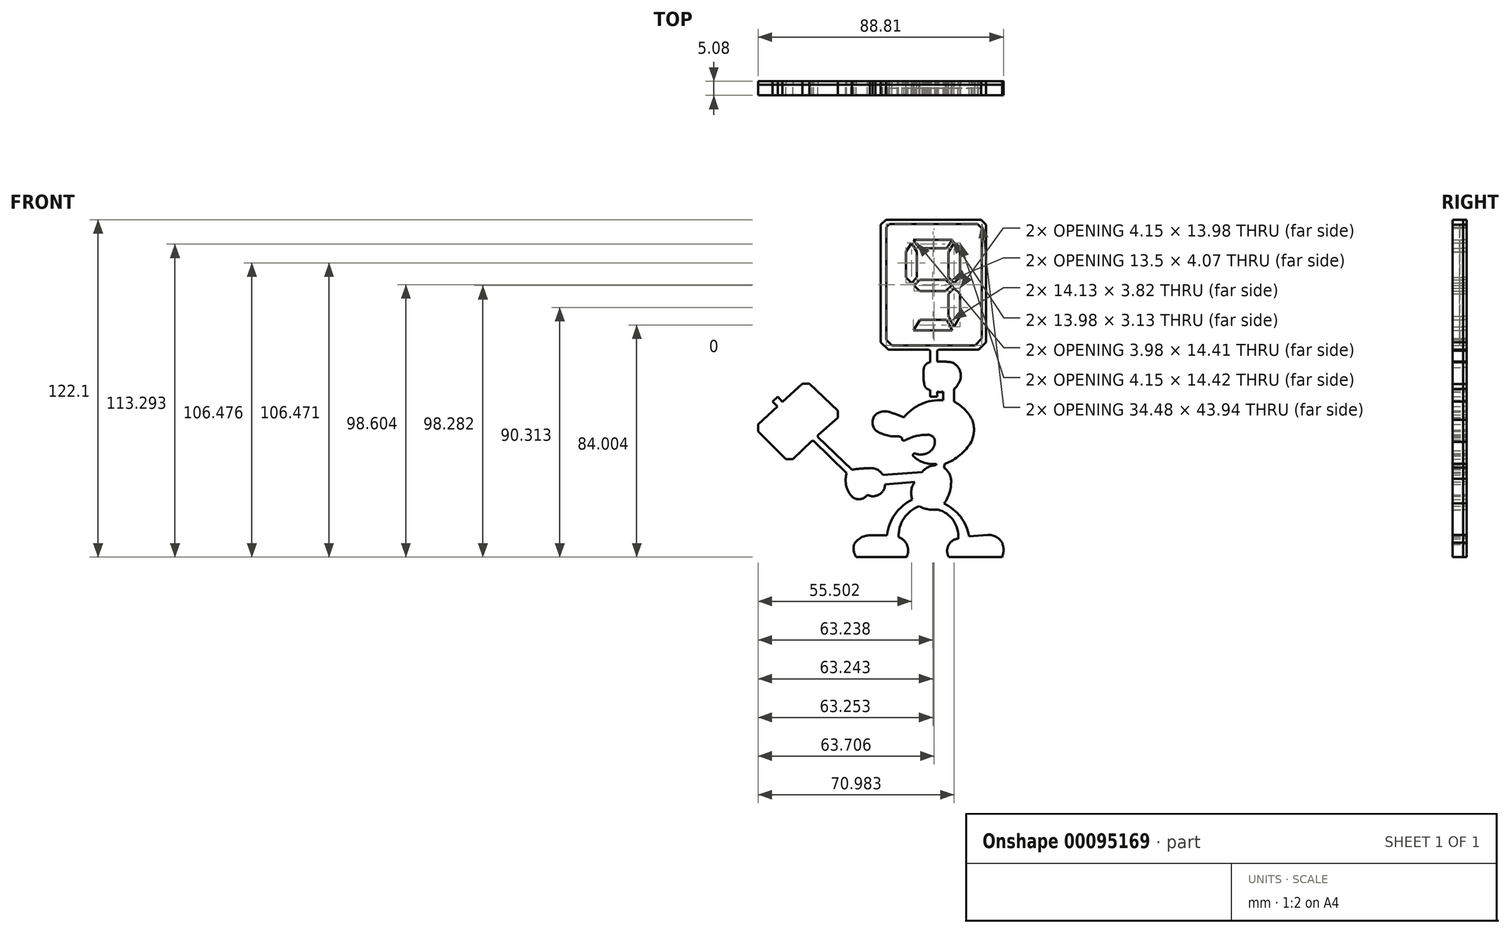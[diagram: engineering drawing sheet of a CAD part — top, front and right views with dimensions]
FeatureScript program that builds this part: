
annotation { "Feature Type Name" : "Feature", "Feature Type Description" : "" }
export const myFeature = defineFeature(function(context is Context, id is Id, definition is map)
    precondition{}
    {
        {
            var Q0;
            Q0=qCreatedBy(makeId("Front.planeOp"),FACE);
            var sketch = newSketch(context, id + "F0", { "sketchPlane" : qUnion([Q0])});
            skLineSegment(sketch, "E0", {"start": v(-24.4, 14.37) * mm, "end": v(-21.86, 14.37) * mm});
            skLineSegment(sketch, "E1", {"start": v(-21.86, 14.37) * mm, "end": v(-11.65, 4.52) * mm});
            skLineSegment(sketch, "E2", {"start": v(-11.65, 4.52) * mm, "end": v(-11.65, 1.98) * mm});
            skLineSegment(sketch, "E3", {"start": v(-24.4, 14.37) * mm, "end": v(-31.63, 7.75) * mm});
            skLineSegment(sketch, "E4", {"start": v(-31.63, 7.75) * mm, "end": v(-33.34, 9.62) * mm});
            skLineSegment(sketch, "E5", {"start": v(-33.34, 9.62) * mm, "end": v(-35.22, 7.9) * mm});
            skLineSegment(sketch, "E6", {"start": v(-35.22, 7.9) * mm, "end": v(-33.5, 6.03) * mm});
            skLineSegment(sketch, "E7", {"start": v(-33.5, 6.03) * mm, "end": v(-40.48, -0.37) * mm});
            skLineSegment(sketch, "E8", {"start": v(-40.48, -0.37) * mm, "end": v(-40.48, -2.9) * mm});
            skLineSegment(sketch, "E9", {"start": v(-40.48, -2.9) * mm, "end": v(-30.45, -12.94) * mm});
            skLineSegment(sketch, "E10", {"start": v(-30.45, -12.94) * mm, "end": v(-27.91, -12.94) * mm});
            skLineSegment(sketch, "E11", {"start": v(-27.91, -12.94) * mm, "end": v(-21, -6.38) * mm});
            skLineSegment(sketch, "E12", {"start": v(-21, -6.38) * mm, "end": v(-20.37, -6.38) * mm});
            skLineSegment(sketch, "E13", {"start": v(-20.37, -6.38) * mm, "end": v(-8.39, -18) * mm});
            skLineSegment(sketch, "E14", {"start": v(-11.65, 1.98) * mm, "end": v(-18.8, -4.32) * mm});
            skLineSegment(sketch, "E15", {"start": v(-18.8, -4.32) * mm, "end": v(-18.8, -4.95) * mm});
            skLineSegment(sketch, "E16", {"start": v(-18.8, -4.95) * mm, "end": v(-6.57, -16.8) * mm});
            skArc(sketch, "E17", {"start": v(-8.39, -18) * mm, "mid": v(-8.63, -22.18) * mm, "end": v(-6.9, -26) * mm});
            skArc(sketch, "E18", {"start": v(-6.9, -26) * mm, "mid": v(-3.9, -27.5) * mm, "end": v(-0.98, -25.87) * mm});
            skArc(sketch, "E19", {"start": v(-0.98, -25.87) * mm, "mid": v(3.31, -25.8) * mm, "end": v(5.5, -22.09) * mm});
            skArc(sketch, "E20", {"start": v(4.68, -18.71) * mm, "mid": v(2.7, -16.78) * mm, "end": v(0, -16.22) * mm});
            skArc(sketch, "E21", {"start": v(0, -16.22) * mm, "mid": v(-3.3, -16.4) * mm, "end": v(-6.57, -16.8) * mm});
            skLineSegment(sketch, "E22", {"start": v(5.5, -22.09) * mm, "end": v(16.16, -21.27) * mm});
            skLineSegment(sketch, "E23", {"start": v(4.68, -18.71) * mm, "end": v(18.9, -17.62) * mm});
            skArc(sketch, "E24", {"start": v(23.92, -15.16) * mm, "mid": v(21.14, -15.83) * mm, "end": v(18.9, -17.62) * mm});
            skArc(sketch, "E25", {"start": v(16.16, -21.27) * mm, "mid": v(14.99, -24.34) * mm, "end": v(15.36, -27.61) * mm});
            skArc(sketch, "E26", {"start": v(15.36, -27.61) * mm, "mid": v(9.1, -32.89) * mm, "end": v(6.19, -40.54) * mm});
            skLineSegment(sketch, "E27", {"start": v(6.19, -40.54) * mm, "end": v(0, -40.54) * mm});
            skArc(sketch, "E28", {"start": v(0, -40.54) * mm, "mid": v(-3.28, -41.41) * mm, "end": v(-5.7, -43.8) * mm});
            skArc(sketch, "E29", {"start": v(-5.7, -43.8) * mm, "mid": v(-5.84, -46.17) * mm, "end": v(-4.97, -48.37) * mm});
            skLineSegment(sketch, "E30", {"start": v(-4.97, -48.37) * mm, "end": v(13.24, -48.37) * mm});
            skArc(sketch, "E31", {"start": v(17.86, -30) * mm, "mid": v(12.3, -34.38) * mm, "end": v(10.44, -41.21) * mm});
            skArc(sketch, "E32", {"start": v(13.24, -48.37) * mm, "mid": v(13.48, -44.15) * mm, "end": v(10.44, -41.21) * mm});
            skArc(sketch, "E33", {"start": v(17.86, -30) * mm, "mid": v(21.1, -31.15) * mm, "end": v(24.55, -31.2) * mm});
            skArc(sketch, "E34", {"start": v(31.92, -41.73) * mm, "mid": v(30.16, -35.12) * mm, "end": v(24.55, -31.2) * mm});
            skArc(sketch, "E35", {"start": v(31.92, -41.73) * mm, "mid": v(28.42, -44.16) * mm, "end": v(28.55, -48.42) * mm});
            skLineSegment(sketch, "E36", {"start": v(28.55, -48.42) * mm, "end": v(47.8, -48.42) * mm});
            skArc(sketch, "E37", {"start": v(47.8, -48.42) * mm, "mid": v(48.33, -45.8) * mm, "end": v(47.8, -43.18) * mm});
            skArc(sketch, "E38", {"start": v(47.8, -43.18) * mm, "mid": v(45.59, -41.04) * mm, "end": v(42.58, -40.4) * mm});
            skLineSegment(sketch, "E39", {"start": v(42.58, -40.4) * mm, "end": v(35.9, -40.92) * mm});
            skArc(sketch, "E40", {"start": v(35.9, -40.92) * mm, "mid": v(32.81, -33.85) * mm, "end": v(26.8, -29.02) * mm});
            skArc(sketch, "E41", {"start": v(26.8, -29.02) * mm, "mid": v(28.88, -24.8) * mm, "end": v(29.34, -20.11) * mm});
            skArc(sketch, "E42", {"start": v(29.34, -20.11) * mm, "mid": v(28.45, -17.81) * mm, "end": v(26.75, -16.02) * mm});
            skLineSegment(sketch, "E43", {"start": v(26.75, -16.02) * mm, "end": v(27.2, -14.67) * mm});
            skLineSegment(sketch, "E44", {"start": v(23.92, -15.16) * mm, "end": v(24.08, -14.67) * mm});
            skArc(sketch, "E45", {"start": v(15.64, -11.86) * mm, "mid": v(19.54, -14.23) * mm, "end": v(24.08, -14.67) * mm});
            skArc(sketch, "E46", {"start": v(16.63, -11.06) * mm, "mid": v(15.8, -11.04) * mm, "end": v(15.64, -11.86) * mm});
            skArc(sketch, "E47", {"start": v(16.63, -11.06) * mm, "mid": v(18.4, -11.3) * mm, "end": v(20.17, -11.06) * mm});
            skArc(sketch, "E48", {"start": v(20.17, -11.06) * mm, "mid": v(21.23, -10.57) * mm, "end": v(22.15, -9.86) * mm});
            skArc(sketch, "E49", {"start": v(22.15, -9.86) * mm, "mid": v(23.3, -8.08) * mm, "end": v(23.43, -5.97) * mm});
            skArc(sketch, "E50", {"start": v(23.43, -5.97) * mm, "mid": v(22.43, -4.56) * mm, "end": v(20.75, -4.14) * mm});
            skArc(sketch, "E51", {"start": v(20.75, -4.14) * mm, "mid": v(16.7, -4.62) * mm, "end": v(12.88, -6.05) * mm});
            skArc(sketch, "E52", {"start": v(2, -2.46) * mm, "mid": v(5.72, -4.24) * mm, "end": v(9.83, -4.73) * mm});
            skArc(sketch, "E53", {"start": v(2, 3.1) * mm, "mid": v(0.93, 0.32) * mm, "end": v(2, -2.46) * mm});
            skArc(sketch, "E54", {"start": v(7.25, 4.03) * mm, "mid": v(4.5, 4.27) * mm, "end": v(2, 3.1) * mm});
            skArc(sketch, "E55", {"start": v(12.32, 2.17) * mm, "mid": v(9.8, 3.15) * mm, "end": v(7.25, 4.03) * mm});
            skArc(sketch, "E56", {"start": v(26.47, 8.35) * mm, "mid": v(18.62, 7.02) * mm, "end": v(12.32, 2.17) * mm});
            skArc(sketch, "E57", {"start": v(11.6, -5.25) * mm, "mid": v(10.76, -4.82) * mm, "end": v(9.83, -4.73) * mm});
            skArc(sketch, "E58", {"start": v(11.6, -6.03) * mm, "mid": v(11.65, -5.64) * mm, "end": v(11.6, -5.25) * mm});
            skArc(sketch, "E59", {"start": v(11.6, -6.03) * mm, "mid": v(12.24, -6.22) * mm, "end": v(12.88, -6.05) * mm});
            skLineSegment(sketch, "E60", {"start": v(30.42, 7.87) * mm, "end": v(30.42, 12.42) * mm});
            skLineSegment(sketch, "E61", {"start": v(26.47, 8.35) * mm, "end": v(26.47, 11.39) * mm});
            skLineSegment(sketch, "E62", {"start": v(24.8, 26.69) * mm, "end": v(39.36, 26.69) * mm});
            skLineSegment(sketch, "E63", {"start": v(39.36, 26.69) * mm, "end": v(42.05, 29.38) * mm});
            skLineSegment(sketch, "E64", {"start": v(42.05, 29.38) * mm, "end": v(42.05, 73.68) * mm});
            skLineSegment(sketch, "E65", {"start": v(42.05, 73.68) * mm, "end": v(3.95, 73.68) * mm});
            skLineSegment(sketch, "E66", {"start": v(3.95, 26.69) * mm, "end": v(21.32, 26.69) * mm});
            skLineSegment(sketch, "E67", {"start": v(21.32, 26.69) * mm, "end": v(21.77, 26.24) * mm});
            skLineSegment(sketch, "E68", {"start": v(21.77, 26.24) * mm, "end": v(21.77, 9.6) * mm});
            skLineSegment(sketch, "E69", {"start": v(21.77, 9.6) * mm, "end": v(24.35, 9.6) * mm});
            skLineSegment(sketch, "E70", {"start": v(24.35, 9.6) * mm, "end": v(24.35, 26.24) * mm});
            skLineSegment(sketch, "E71", {"start": v(24.8, 26.69) * mm, "end": v(24.35, 26.24) * mm});
            skArc(sketch, "E72", {"start": v(20.34, 12.68) * mm, "mid": v(23.3, 11.57) * mm, "end": v(26.47, 11.39) * mm});
            skArc(sketch, "E73", {"start": v(19.56, 20.16) * mm, "mid": v(19.34, 17.1) * mm, "end": v(19.68, 14.07) * mm});
            skArc(sketch, "E74", {"start": v(19.68, 14.07) * mm, "mid": v(19.93, 13.34) * mm, "end": v(20.34, 12.68) * mm});
            skLineSegment(sketch, "E75", {"start": v(40.26, 73.68) * mm, "end": v(42.05, 71.88) * mm});
            skLineSegment(sketch, "E76", {"start": v(3.95, 26.69) * mm, "end": v(3.95, 73.68) * mm});
            skLineSegment(sketch, "E77", {"start": v(5.75, 73.68) * mm, "end": v(3.95, 71.88) * mm});
            skLineSegment(sketch, "E78", {"start": v(3.95, 29.38) * mm, "end": v(6.65, 26.69) * mm});
            skLineSegment(sketch, "E79", {"start": v(42.05, 73.68) * mm, "end": v(42.05, 26.69) * mm});
            skLineSegment(sketch, "E80", {"start": v(42.05, 26.69) * mm, "end": v(39.36, 26.69) * mm});
            skLineSegment(sketch, "E81", {"start": v(38.9, 72.15) * mm, "end": v(40.47, 70.6) * mm});
            skLineSegment(sketch, "E82", {"start": v(40.47, 70.6) * mm, "end": v(40.47, 30.67) * mm});
            skLineSegment(sketch, "E83", {"start": v(40.47, 30.67) * mm, "end": v(38.01, 28.21) * mm});
            skLineSegment(sketch, "E84", {"start": v(38.01, 28.21) * mm, "end": v(8, 28.21) * mm});
            skLineSegment(sketch, "E85", {"start": v(8, 28.21) * mm, "end": v(5.99, 30.22) * mm});
            skLineSegment(sketch, "E86", {"start": v(5.99, 30.22) * mm, "end": v(5.99, 71.04) * mm});
            skLineSegment(sketch, "E87", {"start": v(5.99, 71.04) * mm, "end": v(7.1, 72.15) * mm});
            skLineSegment(sketch, "E88", {"start": v(7.1, 72.15) * mm, "end": v(38.9, 72.15) * mm});
            skArc(sketch, "E89", {"start": v(27.2, -14.67) * mm, "mid": v(32.6, -11.48) * mm, "end": v(36.69, -6.71) * mm});
            skArc(sketch, "E90", {"start": v(36.69, -6.71) * mm, "mid": v(37.64, -2.76) * mm, "end": v(37, 1.25) * mm});
            skArc(sketch, "E91", {"start": v(37, 1.25) * mm, "mid": v(34.24, 5.1) * mm, "end": v(30.42, 7.87) * mm});
            skLineSegment(sketch, "E92", {"start": v(15.77, 66.44) * mm, "end": v(29.75, 66.44) * mm});
            skLineSegment(sketch, "E93", {"start": v(29.75, 66.44) * mm, "end": v(27.76, 63.3) * mm});
            skLineSegment(sketch, "E94", {"start": v(27.76, 63.3) * mm, "end": v(17.76, 63.3) * mm});
            skLineSegment(sketch, "E95", {"start": v(17.76, 63.3) * mm, "end": v(15.77, 66.44) * mm});
            skLineSegment(sketch, "E96", {"start": v(30.5, 65.26) * mm, "end": v(28.43, 62) * mm});
            skLineSegment(sketch, "E97", {"start": v(28.43, 62) * mm, "end": v(28.43, 52.88) * mm});
            skLineSegment(sketch, "E98", {"start": v(28.43, 52.88) * mm, "end": v(30.5, 50.84) * mm});
            skLineSegment(sketch, "E99", {"start": v(30.5, 50.84) * mm, "end": v(32.58, 52.88) * mm});
            skLineSegment(sketch, "E100", {"start": v(32.58, 52.88) * mm, "end": v(32.58, 62) * mm});
            skLineSegment(sketch, "E101", {"start": v(32.58, 62) * mm, "end": v(30.5, 65.26) * mm});
            skLineSegment(sketch, "E102", {"start": v(29.5, 49.86) * mm, "end": v(27.43, 51.9) * mm});
            skLineSegment(sketch, "E103", {"start": v(27.43, 51.9) * mm, "end": v(18.05, 51.9) * mm});
            skLineSegment(sketch, "E104", {"start": v(18.05, 51.9) * mm, "end": v(16.01, 49.86) * mm});
            skLineSegment(sketch, "E105", {"start": v(16.01, 49.86) * mm, "end": v(18.05, 47.83) * mm});
            skLineSegment(sketch, "E106", {"start": v(18.05, 47.83) * mm, "end": v(27.43, 47.83) * mm});
            skLineSegment(sketch, "E107", {"start": v(27.43, 47.83) * mm, "end": v(29.5, 49.86) * mm});
            skLineSegment(sketch, "E108", {"start": v(17.01, 52.84) * mm, "end": v(15.02, 50.85) * mm});
            skLineSegment(sketch, "E109", {"start": v(15.02, 50.85) * mm, "end": v(13.03, 52.84) * mm});
            skLineSegment(sketch, "E110", {"start": v(13.03, 52.84) * mm, "end": v(13.03, 62.13) * mm});
            skLineSegment(sketch, "E111", {"start": v(13.03, 62.13) * mm, "end": v(15.02, 65.26) * mm});
            skLineSegment(sketch, "E112", {"start": v(15.02, 65.26) * mm, "end": v(17.01, 62.13) * mm});
            skLineSegment(sketch, "E113", {"start": v(17.01, 62.13) * mm, "end": v(17.01, 52.84) * mm});
            skLineSegment(sketch, "E114", {"start": v(29.84, 33.67) * mm, "end": v(27.76, 37.5) * mm});
            skLineSegment(sketch, "E115", {"start": v(27.76, 37.5) * mm, "end": v(18.09, 37.5) * mm});
            skLineSegment(sketch, "E116", {"start": v(18.09, 37.5) * mm, "end": v(15.71, 33.67) * mm});
            skLineSegment(sketch, "E117", {"start": v(15.71, 33.67) * mm, "end": v(29.84, 33.67) * mm});
            skLineSegment(sketch, "E118", {"start": v(30.5, 34.9) * mm, "end": v(28.43, 38.72) * mm});
            skLineSegment(sketch, "E119", {"start": v(28.43, 38.72) * mm, "end": v(28.43, 46.85) * mm});
            skLineSegment(sketch, "E120", {"start": v(28.43, 46.85) * mm, "end": v(30.5, 48.88) * mm});
            skLineSegment(sketch, "E121", {"start": v(30.5, 48.88) * mm, "end": v(32.58, 46.85) * mm});
            skLineSegment(sketch, "E122", {"start": v(32.58, 46.85) * mm, "end": v(32.58, 38.72) * mm});
            skLineSegment(sketch, "E123", {"start": v(32.58, 38.72) * mm, "end": v(30.5, 34.9) * mm});
            skLineSegment(sketch, "E124", {"start": v(28.43, 46.85) * mm, "end": v(32.58, 46.85) * mm});
            skLineSegment(sketch, "E125", {"start": v(13.03, 62.13) * mm, "end": v(15.77, 66.44) * mm});
            skLineSegment(sketch, "E126", {"start": v(32.58, 62) * mm, "end": v(29.75, 66.44) * mm});
            skLineSegment(sketch, "E127", {"start": v(13.03, 62.13) * mm, "end": v(17.01, 62.13) * mm});
            skLineSegment(sketch, "E128", {"start": v(28.43, 62) * mm, "end": v(32.58, 62) * mm});
            skLineSegment(sketch, "E129", {"start": v(18.05, 51.9) * mm, "end": v(18.05, 47.83) * mm});
            skLineSegment(sketch, "E130", {"start": v(29.84, 33.67) * mm, "end": v(32.58, 38.72) * mm});
            skLineSegment(sketch, "E131", {"start": v(27.76, 37.5) * mm, "end": v(28.95, 39.68) * mm});
            skLineSegment(sketch, "E132", {"start": v(32.58, 46.85) * mm, "end": v(27.43, 51.9) * mm});
            skLineSegment(sketch, "E133", {"start": v(28.43, 46.85) * mm, "end": v(24.6, 50.6) * mm});
            skLineSegment(sketch, "E134", {"start": v(18.05, 51.9) * mm, "end": v(14.3, 55.32) * mm});
            skLineSegment(sketch, "E135", {"start": v(27.43, 47.83) * mm, "end": v(32.58, 52.88) * mm});
            skLineSegment(sketch, "E136", {"start": v(17.01, 62.13) * mm, "end": v(19.33, 65.77) * mm});
            skLineSegment(sketch, "E137", {"start": v(28.43, 62) * mm, "end": v(25.65, 66.37) * mm});
            skLineSegment(sketch, "E138", {"start": v(27.43, 51.9) * mm, "end": v(30.99, 55.39) * mm});
            skLineSegment(sketch, "E139", {"start": v(30.5, 48.88) * mm, "end": v(30.5, 50.84) * mm});
            skArc(sketch, "E140", {"start": v(21.77, 22.1) * mm, "mid": v(20.4, 21.43) * mm, "end": v(19.56, 20.16) * mm});
            skArc(sketch, "E141", {"start": v(29.58, 22.1) * mm, "mid": v(25.67, 22.35) * mm, "end": v(21.77, 22.1) * mm});
            skArc(sketch, "E142", {"start": v(31.9, 14.23) * mm, "mid": v(32.67, 18.73) * mm, "end": v(29.58, 22.1) * mm});
            skArc(sketch, "E143", {"start": v(30.42, 12.42) * mm, "mid": v(31.29, 13.22) * mm, "end": v(31.9, 14.23) * mm});
            skLineSegment(sketch, "E144", {"start": v(15.02, 50.85) * mm, "end": v(16.01, 49.86) * mm});
            skSolve(sketch);
        }
        {
            var Q0;
            Q0=makeQuery(id+"F0.imprint","IMPRINT",FACE,{"disambiguationData":[TD([[makeQuery(id+"F0.imprint","IMPRINT",EDGE,{"derivedFrom":sQuery(id+"F0.wireOp",EDGE,"E0")}),-1.0]])]});
            var Q1;
            {var subQ3=sQuery(id+"F0.wireOp",EDGE,"E72");var subQ5=sQuery(id+"F0.wireOp",EDGE,"E70");var subQ6=makeQuery(id+"F0.imprint","INTERSECT",VERTEX,{"derivedFrom":[subQ5,subQ3]});Q1=makeQuery(id+"F0.imprint","IMPRINT",FACE,{"disambiguationData":[TD([[makeQuery(id+"F0.imprint","IMPRINT",EDGE,{"disambiguationData":[TD([[subQ6,-1.0]])],"derivedFrom":subQ5}),1.0]])]});}
            var Q2;
            Q2=makeQuery(id+"F0.imprint","IMPRINT",FACE,{"disambiguationData":[TD([[makeQuery(id+"F0.imprint","IMPRINT",EDGE,{"derivedFrom":sQuery(id+"F0.wireOp",EDGE,"E73")}),1.0]])]});
            var Q3;
            {var subQ0=sQuery(id+"F0.wireOp",EDGE,"E69");Q3=makeQuery(id+"F0.imprint","IMPRINT",FACE,{"disambiguationData":[TD([[makeQuery(id+"F0.imprint","IMPRINT",EDGE,{"derivedFrom":subQ0}),1.0]])]});}
            var Q4;
            Q4=makeQuery(id+"F0.imprint","IMPRINT",FACE,{"disambiguationData":[TD([[makeQuery(id+"F0.imprint","IMPRINT",EDGE,{"derivedFrom":sQuery(id+"F0.wireOp",EDGE,"E62")}),1.0]])]});
            var Q5;
            Q5=makeQuery(id+"F0.imprint","IMPRINT",FACE,{"disambiguationData":[TD([[makeQuery(id+"F0.imprint","IMPRINT",EDGE,{"derivedFrom":sQuery(id+"F0.wireOp",EDGE,"E114")}),1.0]])]});
            var Q6;
            {var subQ2=sQuery(id+"F0.wireOp",EDGE,"E118");Q6=makeQuery(id+"F0.imprint","IMPRINT",FACE,{"disambiguationData":[TD([[makeQuery(id+"F0.imprint","IMPRINT",EDGE,{"derivedFrom":subQ2}),-1.0]])]});}
            var Q7;
            {var subQ0=sQuery(id+"F0.wireOp",EDGE,"E120");Q7=makeQuery(id+"F0.imprint","IMPRINT",FACE,{"disambiguationData":[TD([[makeQuery(id+"F0.imprint","IMPRINT",EDGE,{"derivedFrom":subQ0}),-1.0]])]});}
            var Q8;
            {var subQ1=sQuery(id+"F0.wireOp",EDGE,"E103");Q8=makeQuery(id+"F0.imprint","IMPRINT",FACE,{"disambiguationData":[TD([[makeQuery(id+"F0.imprint","IMPRINT",EDGE,{"derivedFrom":subQ1}),1.0]])]});}
            var Q9;
            {var subQ0=sQuery(id+"F0.wireOp",EDGE,"E104");Q9=makeQuery(id+"F0.imprint","IMPRINT",FACE,{"disambiguationData":[TD([[makeQuery(id+"F0.imprint","IMPRINT",EDGE,{"derivedFrom":subQ0}),1.0]])]});}
            var Q10;
            {var subQ1=sQuery(id+"F0.wireOp",EDGE,"E108");Q10=makeQuery(id+"F0.imprint","IMPRINT",FACE,{"disambiguationData":[TD([[makeQuery(id+"F0.imprint","IMPRINT",EDGE,{"derivedFrom":subQ1}),-1.0]])]});}
            var Q11;
            {var subQ0=sQuery(id+"F0.wireOp",EDGE,"E112");Q11=makeQuery(id+"F0.imprint","IMPRINT",FACE,{"disambiguationData":[TD([[makeQuery(id+"F0.imprint","IMPRINT",EDGE,{"derivedFrom":subQ0}),-1.0]])]});}
            var Q12;
            Q12=makeQuery(id+"F0.imprint","IMPRINT",FACE,{"disambiguationData":[TD([[makeQuery(id+"F0.imprint","IMPRINT",EDGE,{"derivedFrom":sQuery(id+"F0.wireOp",EDGE,"E92")}),-1.0]])]});
            var Q13;
            {var subQ0=sQuery(id+"F0.wireOp",EDGE,"E96");Q13=makeQuery(id+"F0.imprint","IMPRINT",FACE,{"disambiguationData":[TD([[makeQuery(id+"F0.imprint","IMPRINT",EDGE,{"derivedFrom":subQ0}),1.0]])]});}
            var Q14;
            {var subQ1=sQuery(id+"F0.wireOp",EDGE,"E98");Q14=makeQuery(id+"F0.imprint","IMPRINT",FACE,{"disambiguationData":[TD([[makeQuery(id+"F0.imprint","IMPRINT",EDGE,{"derivedFrom":subQ1}),1.0]])]});}
            extrude(context, id + "F1", {"entities" : qUnion([Q0, Q1, Q2, Q3, Q4, Q5, Q6, Q7, Q8, Q9, Q10, Q11, Q12, Q13, Q14]), "depth" : 3.8 * mm});
        }
        {
            var Q0;
            Q0=makeQuery(id+"F0.imprint","IMPRINT",FACE,{"disambiguationData":[TD([[makeQuery(id+"F0.imprint","IMPRINT",EDGE,{"derivedFrom":sQuery(id+"F0.wireOp",EDGE,"E81")}),-1.0]])]});
            var Q1;
            {var subQ5=sQuery(id+"F0.wireOp",EDGE,"E98");Q1=makeQuery(id+"F0.imprint","IMPRINT",FACE,{"disambiguationData":[TD([[makeQuery(id+"F0.imprint","IMPRINT",EDGE,{"derivedFrom":subQ5}),-1.0]])]});}
            var Q2;
            {var subQ0=sQuery(id+"F0.wireOp",EDGE,"E139");Q2=makeQuery(id+"F0.imprint","IMPRINT",FACE,{"disambiguationData":[TD([[makeQuery(id+"F0.imprint","IMPRINT",EDGE,{"derivedFrom":subQ0}),1.0]])]});}
            var Q3;
            {var subQ0=sQuery(id+"F0.wireOp",EDGE,"E120");Q3=makeQuery(id+"F0.imprint","IMPRINT",FACE,{"disambiguationData":[TD([[makeQuery(id+"F0.imprint","IMPRINT",EDGE,{"derivedFrom":subQ0}),1.0]])]});}
            var Q4;
            {var subQ0=sQuery(id+"F0.wireOp",EDGE,"E114");Q4=makeQuery(id+"F0.imprint","IMPRINT",FACE,{"disambiguationData":[TD([[makeQuery(id+"F0.imprint","IMPRINT",EDGE,{"derivedFrom":subQ0}),-1.0]])]});}
            var Q5;
            {var subQ0=sQuery(id+"F0.wireOp",EDGE,"E104");Q5=makeQuery(id+"F0.imprint","IMPRINT",FACE,{"disambiguationData":[TD([[makeQuery(id+"F0.imprint","IMPRINT",EDGE,{"derivedFrom":subQ0}),-1.0]])]});}
            var Q6;
            {var subQ1=sQuery(id+"F0.wireOp",EDGE,"E103");Q6=makeQuery(id+"F0.imprint","IMPRINT",FACE,{"disambiguationData":[TD([[makeQuery(id+"F0.imprint","IMPRINT",EDGE,{"derivedFrom":subQ1}),-1.0]])]});}
            var Q7;
            {var subQ0=sQuery(id+"F0.wireOp",EDGE,"E95");Q7=makeQuery(id+"F0.imprint","IMPRINT",FACE,{"disambiguationData":[TD([[makeQuery(id+"F0.imprint","IMPRINT",EDGE,{"derivedFrom":subQ0}),1.0]])]});}
            var Q8;
            {var subQ1=sQuery(id+"F0.wireOp",EDGE,"E93");Q8=makeQuery(id+"F0.imprint","IMPRINT",FACE,{"disambiguationData":[TD([[makeQuery(id+"F0.imprint","IMPRINT",EDGE,{"derivedFrom":subQ1}),1.0]])]});}
            extrude(context, id + "F2", {"entities" : qUnion([Q0, Q1, Q2, Q3, Q4, Q5, Q6, Q7, Q8]), "depth" : 1.27 * mm});
        }
        {
            var Q0;
            Q0=makeQuery(id+"F1.opExtrude","CAP_FACE",FACE,{"disambiguationData":[OSD([sQuery(id+"F0.wireOp",EDGE,"E96"),sQuery(id+"F0.wireOp",EDGE,"E97"),sQuery(id+"F0.wireOp",EDGE,"E98"),sQuery(id+"F0.wireOp",EDGE,"E100"),sQuery(id+"F0.wireOp",EDGE,"E126"),sQuery(id+"F0.wireOp",EDGE,"E135")])],"isStart":true});
            var Q1;
            Q1=makeQuery(id+"F1.opExtrude","CAP_FACE",FACE,{"disambiguationData":[OSD([sQuery(id+"F0.wireOp",EDGE,"E92"),sQuery(id+"F0.wireOp",EDGE,"E93"),sQuery(id+"F0.wireOp",EDGE,"E94"),sQuery(id+"F0.wireOp",EDGE,"E95")])],"isStart":true});
            var Q2;
            Q2=makeQuery(id+"F1.opExtrude","CAP_FACE",FACE,{"disambiguationData":[OSD([sQuery(id+"F0.wireOp",EDGE,"E108"),sQuery(id+"F0.wireOp",EDGE,"E110"),sQuery(id+"F0.wireOp",EDGE,"E112"),sQuery(id+"F0.wireOp",EDGE,"E113"),sQuery(id+"F0.wireOp",EDGE,"nikI6qLt-cf0r-R0Sj-jdNE-G8wGwsvtiRU5"),sQuery(id+"F0.wireOp",EDGE,"E125")])],"isStart":true});
            var Q3;
            Q3=makeQuery(id+"F1.opExtrude","CAP_FACE",FACE,{"disambiguationData":[OSD([sQuery(id+"F0.wireOp",EDGE,"E103"),sQuery(id+"F0.wireOp",EDGE,"E104"),sQuery(id+"F0.wireOp",EDGE,"E106"),sQuery(id+"F0.wireOp",EDGE,"nikI6qLt-cf0r-R0Sj-jdNE-G8wGwsvtiRU5"),sQuery(id+"F0.wireOp",EDGE,"E132"),sQuery(id+"F0.wireOp",EDGE,"E135")])],"isStart":true});
            var Q4;
            Q4=makeQuery(id+"F1.opExtrude","CAP_FACE",FACE,{"disambiguationData":[OSD([sQuery(id+"F0.wireOp",EDGE,"E118"),sQuery(id+"F0.wireOp",EDGE,"E119"),sQuery(id+"F0.wireOp",EDGE,"E120"),sQuery(id+"F0.wireOp",EDGE,"E122"),sQuery(id+"F0.wireOp",EDGE,"E130"),sQuery(id+"F0.wireOp",EDGE,"E132")])],"isStart":true});
            var Q5;
            Q5=makeQuery(id+"F1.opExtrude","CAP_FACE",FACE,{"disambiguationData":[OSD([sQuery(id+"F0.wireOp",EDGE,"E114"),sQuery(id+"F0.wireOp",EDGE,"E115"),sQuery(id+"F0.wireOp",EDGE,"E116"),sQuery(id+"F0.wireOp",EDGE,"E117")])],"isStart":true});
            var Q6;
            Q6=makeQuery(id+"F2.opExtrude","CAP_FACE",FACE,{"disambiguationData":[OSD([sQuery(id+"F0.wireOp",EDGE,"E81"),sQuery(id+"F0.wireOp",EDGE,"E82"),sQuery(id+"F0.wireOp",EDGE,"E83"),sQuery(id+"F0.wireOp",EDGE,"E84"),sQuery(id+"F0.wireOp",EDGE,"E85"),sQuery(id+"F0.wireOp",EDGE,"E86"),sQuery(id+"F0.wireOp",EDGE,"E87"),sQuery(id+"F0.wireOp",EDGE,"E88"),sQuery(id+"F0.wireOp",EDGE,"E92"),sQuery(id+"F0.wireOp",EDGE,"E93"),sQuery(id+"F0.wireOp",EDGE,"E94"),sQuery(id+"F0.wireOp",EDGE,"E95"),sQuery(id+"F0.wireOp",EDGE,"E96"),sQuery(id+"F0.wireOp",EDGE,"E97"),sQuery(id+"F0.wireOp",EDGE,"E98"),sQuery(id+"F0.wireOp",EDGE,"E100"),sQuery(id+"F0.wireOp",EDGE,"E103"),sQuery(id+"F0.wireOp",EDGE,"E104"),sQuery(id+"F0.wireOp",EDGE,"E106"),sQuery(id+"F0.wireOp",EDGE,"E108"),sQuery(id+"F0.wireOp",EDGE,"E110"),sQuery(id+"F0.wireOp",EDGE,"E112"),sQuery(id+"F0.wireOp",EDGE,"E113"),sQuery(id+"F0.wireOp",EDGE,"E114"),sQuery(id+"F0.wireOp",EDGE,"E115"),sQuery(id+"F0.wireOp",EDGE,"E116"),sQuery(id+"F0.wireOp",EDGE,"E117"),sQuery(id+"F0.wireOp",EDGE,"E118"),sQuery(id+"F0.wireOp",EDGE,"E119"),sQuery(id+"F0.wireOp",EDGE,"E120"),sQuery(id+"F0.wireOp",EDGE,"E122"),sQuery(id+"F0.wireOp",EDGE,"nikI6qLt-cf0r-R0Sj-jdNE-G8wGwsvtiRU5"),sQuery(id+"F0.wireOp",EDGE,"E125"),sQuery(id+"F0.wireOp",EDGE,"E126"),sQuery(id+"F0.wireOp",EDGE,"E130"),sQuery(id+"F0.wireOp",EDGE,"E132"),sQuery(id+"F0.wireOp",EDGE,"E135")])],"isStart":true});
            var Q7;
            Q7=makeQuery(id+"F1.opExtrude","CAP_FACE",FACE,{"disambiguationData":[OSD([sQuery(id+"F0.wireOp",EDGE,"E0"),sQuery(id+"F0.wireOp",EDGE,"E1"),sQuery(id+"F0.wireOp",EDGE,"E2"),sQuery(id+"F0.wireOp",EDGE,"E3"),sQuery(id+"F0.wireOp",EDGE,"E4"),sQuery(id+"F0.wireOp",EDGE,"E5"),sQuery(id+"F0.wireOp",EDGE,"E6"),sQuery(id+"F0.wireOp",EDGE,"E7"),sQuery(id+"F0.wireOp",EDGE,"E8"),sQuery(id+"F0.wireOp",EDGE,"E9"),sQuery(id+"F0.wireOp",EDGE,"E10"),sQuery(id+"F0.wireOp",EDGE,"E11"),sQuery(id+"F0.wireOp",EDGE,"E12"),sQuery(id+"F0.wireOp",EDGE,"E13"),sQuery(id+"F0.wireOp",EDGE,"E14"),sQuery(id+"F0.wireOp",EDGE,"E15"),sQuery(id+"F0.wireOp",EDGE,"E16"),sQuery(id+"F0.wireOp",EDGE,"E17"),sQuery(id+"F0.wireOp",EDGE,"E18"),sQuery(id+"F0.wireOp",EDGE,"E19"),sQuery(id+"F0.wireOp",EDGE,"E20"),sQuery(id+"F0.wireOp",EDGE,"E21"),sQuery(id+"F0.wireOp",EDGE,"E22"),sQuery(id+"F0.wireOp",EDGE,"E23"),sQuery(id+"F0.wireOp",EDGE,"E24"),sQuery(id+"F0.wireOp",EDGE,"E25"),sQuery(id+"F0.wireOp",EDGE,"E26"),sQuery(id+"F0.wireOp",EDGE,"E27"),sQuery(id+"F0.wireOp",EDGE,"E28"),sQuery(id+"F0.wireOp",EDGE,"E29"),sQuery(id+"F0.wireOp",EDGE,"E30"),sQuery(id+"F0.wireOp",EDGE,"E31"),sQuery(id+"F0.wireOp",EDGE,"E32"),sQuery(id+"F0.wireOp",EDGE,"E33"),sQuery(id+"F0.wireOp",EDGE,"E34"),sQuery(id+"F0.wireOp",EDGE,"E35"),sQuery(id+"F0.wireOp",EDGE,"E36"),sQuery(id+"F0.wireOp",EDGE,"E37"),sQuery(id+"F0.wireOp",EDGE,"E38"),sQuery(id+"F0.wireOp",EDGE,"E39"),sQuery(id+"F0.wireOp",EDGE,"E40"),sQuery(id+"F0.wireOp",EDGE,"E41"),sQuery(id+"F0.wireOp",EDGE,"E42"),sQuery(id+"F0.wireOp",EDGE,"E43"),sQuery(id+"F0.wireOp",EDGE,"E44"),sQuery(id+"F0.wireOp",EDGE,"E45"),sQuery(id+"F0.wireOp",EDGE,"E46"),sQuery(id+"F0.wireOp",EDGE,"E47"),sQuery(id+"F0.wireOp",EDGE,"E48"),sQuery(id+"F0.wireOp",EDGE,"E49"),sQuery(id+"F0.wireOp",EDGE,"E50"),sQuery(id+"F0.wireOp",EDGE,"E51"),sQuery(id+"F0.wireOp",EDGE,"E52"),sQuery(id+"F0.wireOp",EDGE,"E53"),sQuery(id+"F0.wireOp",EDGE,"E54"),sQuery(id+"F0.wireOp",EDGE,"E55"),sQuery(id+"F0.wireOp",EDGE,"E56"),sQuery(id+"F0.wireOp",EDGE,"E57"),sQuery(id+"F0.wireOp",EDGE,"E58"),sQuery(id+"F0.wireOp",EDGE,"E59"),sQuery(id+"F0.wireOp",EDGE,"E60"),sQuery(id+"F0.wireOp",EDGE,"E61"),sQuery(id+"F0.wireOp",EDGE,"E62"),sQuery(id+"F0.wireOp",EDGE,"E63"),sQuery(id+"F0.wireOp",EDGE,"E65"),sQuery(id+"F0.wireOp",EDGE,"E66"),sQuery(id+"F0.wireOp",EDGE,"E67"),sQuery(id+"F0.wireOp",EDGE,"E68"),sQuery(id+"F0.wireOp",EDGE,"E69"),sQuery(id+"F0.wireOp",EDGE,"E70"),sQuery(id+"F0.wireOp",EDGE,"E71"),sQuery(id+"F0.wireOp",EDGE,"E72"),sQuery(id+"F0.wireOp",EDGE,"E73"),sQuery(id+"F0.wireOp",EDGE,"E74"),sQuery(id+"F0.wireOp",EDGE,"E75"),sQuery(id+"F0.wireOp",EDGE,"E76"),sQuery(id+"F0.wireOp",EDGE,"E77"),sQuery(id+"F0.wireOp",EDGE,"E78"),sQuery(id+"F0.wireOp",EDGE,"E79"),sQuery(id+"F0.wireOp",EDGE,"E81"),sQuery(id+"F0.wireOp",EDGE,"E82"),sQuery(id+"F0.wireOp",EDGE,"E83"),sQuery(id+"F0.wireOp",EDGE,"E84"),sQuery(id+"F0.wireOp",EDGE,"E85"),sQuery(id+"F0.wireOp",EDGE,"E86"),sQuery(id+"F0.wireOp",EDGE,"E87"),sQuery(id+"F0.wireOp",EDGE,"E88"),sQuery(id+"F0.wireOp",EDGE,"E89"),sQuery(id+"F0.wireOp",EDGE,"E90"),sQuery(id+"F0.wireOp",EDGE,"E91"),sQuery(id+"F0.wireOp",EDGE,"E140"),sQuery(id+"F0.wireOp",EDGE,"E141"),sQuery(id+"F0.wireOp",EDGE,"E142"),sQuery(id+"F0.wireOp",EDGE,"E143")])],"isStart":true});
            extrude(context, id + "F3", {"entities" : qUnion([Q0, Q1, Q2, Q3, Q4, Q5, Q6, Q7]), "depth" : 1.27 * mm});
        }
    });
